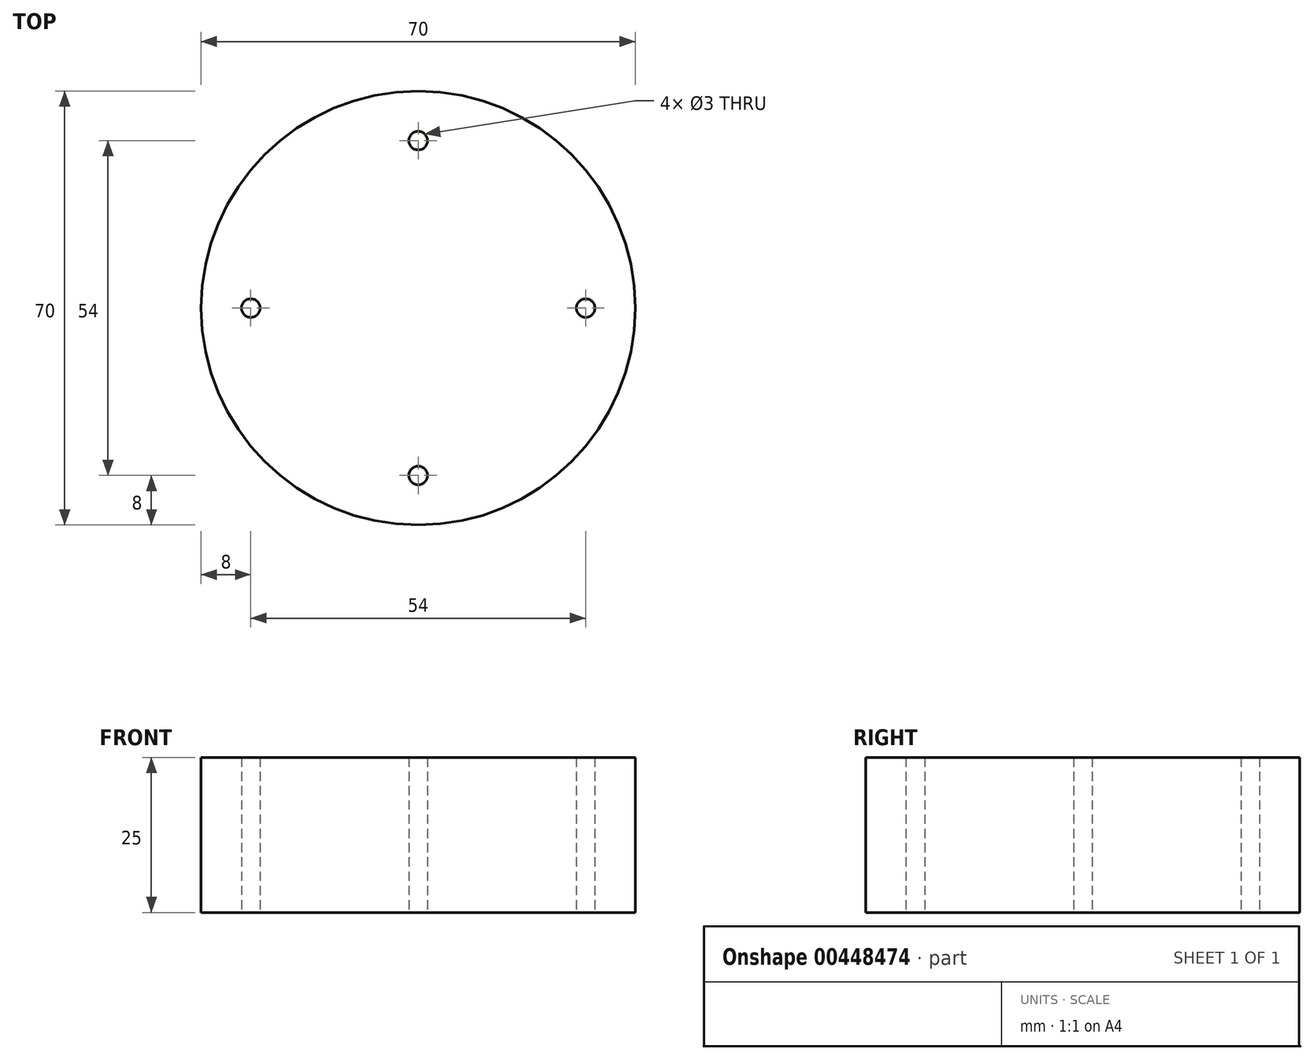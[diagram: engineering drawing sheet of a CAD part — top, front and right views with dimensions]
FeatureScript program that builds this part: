
annotation { "Feature Type Name" : "Feature", "Feature Type Description" : "" }
export const myFeature = defineFeature(function(context is Context, id is Id, definition is map)
    precondition{}
    {
        {
            var Q0;
            Q0=qCreatedBy(makeId("Top.planeOp"),FACE);
            var sketch = newSketch(context, id + "F0", { "sketchPlane" : qUnion([Q0])});
            skCircle(sketch, "E0", {"center": v(0, 0) * mm, "radius": 35 * mm});
            skCircle(sketch, "E1", {"center": v(27, 0) * mm, "radius": 1.5 * mm});
            skCircle(sketch, "E2.1.0", {"center": v(0, -27) * mm, "radius": 1.5 * mm});
            skCircle(sketch, "E2.2.0", {"center": v(-27, 0) * mm, "radius": 1.5 * mm});
            skCircle(sketch, "E2.3.0", {"center": v(0, 27) * mm, "radius": 1.5 * mm});
            skLineSegment(sketch, "E2.anchor1", {"start": v(0, 0) * mm, "end": v(27, 0) * mm, "construction": true});
            skLineSegment(sketch, "E2.anchor2", {"start": v(0, 0) * mm, "end": v(0, 27) * mm, "construction": true});
            skSolve(sketch);
        }
        {
            var Q0;
            Q0=makeQuery(id+"F0.imprint","IMPRINT",FACE,{"disambiguationData":[TD([[makeQuery(id+"F0.imprint","IMPRINT",EDGE,{"derivedFrom":sQuery(id+"F0.wireOp",EDGE,"E0")}),1.0]])]});
            extrude(context, id + "F1", {"entities" : qUnion([Q0]), "depth" : 25 * mm});
        }
    });
